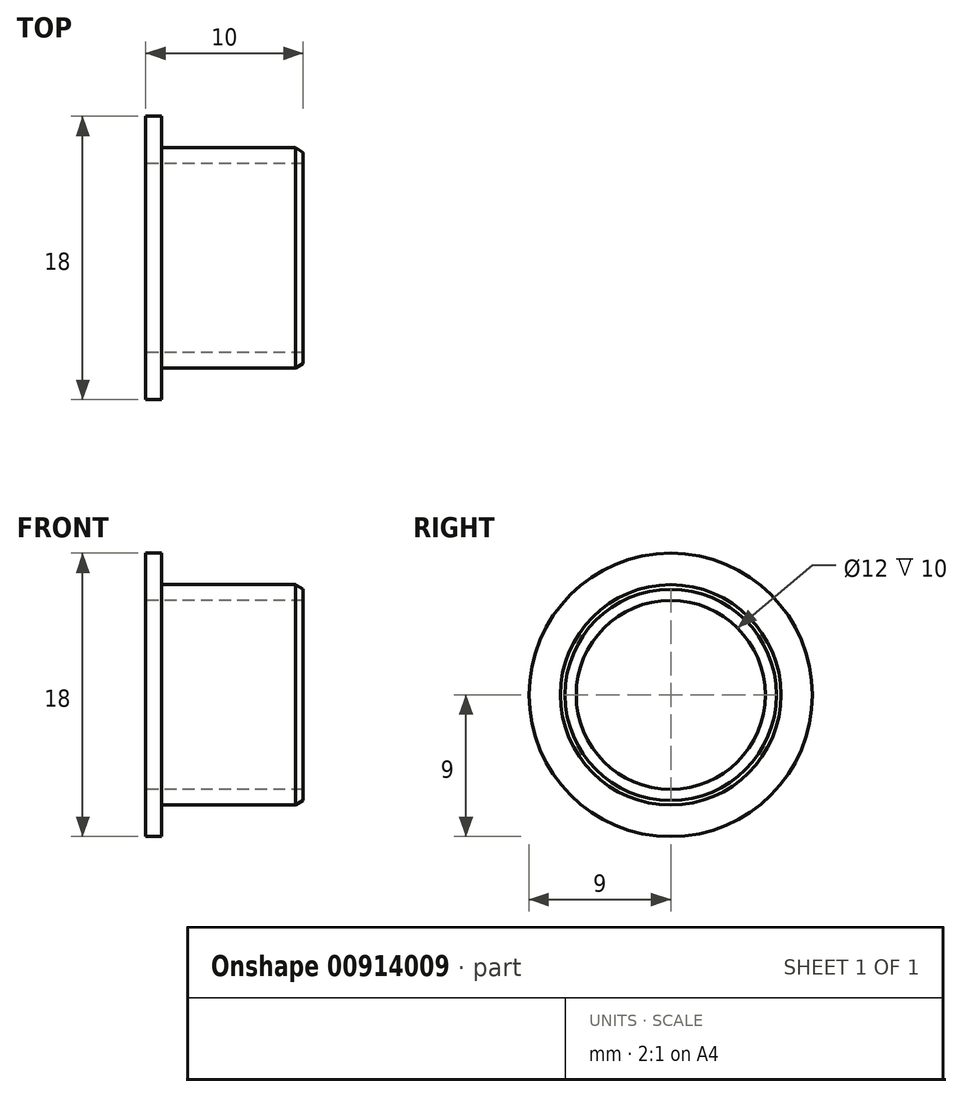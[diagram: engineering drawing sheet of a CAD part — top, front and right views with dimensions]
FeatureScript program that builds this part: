
annotation { "Feature Type Name" : "Feature", "Feature Type Description" : "" }
export const myFeature = defineFeature(function(context is Context, id is Id, definition is map)
    precondition{}
    {
        {
            var Q0;
            Q0=qCreatedBy(makeId("Front.planeOp"),FACE);
            var sketch = newSketch(context, id + "F0", { "sketchPlane" : qUnion([Q0])});
            skLineSegment(sketch, "E0", {"start": v(-14.71, 0) * mm, "end": v(17.2, 0) * mm, "construction": true});
            skLineSegment(sketch, "E1", {"start": v(-1, 9) * mm, "end": v(-1, 6) * mm});
            skLineSegment(sketch, "E2", {"start": v(-1, 6) * mm, "end": v(9, 6) * mm});
            skLineSegment(sketch, "E3", {"start": v(-1, 9) * mm, "end": v(0, 9) * mm});
            skLineSegment(sketch, "E4", {"start": v(0, 9) * mm, "end": v(0, 7) * mm});
            skLineSegment(sketch, "E5", {"start": v(0, 7) * mm, "end": v(8.5, 7) * mm});
            skLineSegment(sketch, "E6", {"start": v(8.5, 7) * mm, "end": v(9, 6.71) * mm});
            skLineSegment(sketch, "E7", {"start": v(9, 6.71) * mm, "end": v(9, 6) * mm});
            skSolve(sketch);
        }
        {
            var Q0;
            Q0=qSketchRegion(id+"F0",true);
            var Q1;
            Q1=sQuery(id+"F0.wireOp",EDGE,"E0");
            revolve(context, id + "F1", {"surfaceOperationType" : NewSurfaceOperationType.NEW, "entities" : qUnion([Q0]), "axis" : qUnion([Q1]), "revolveType" : RevolveType.FULL});
        }
    });
